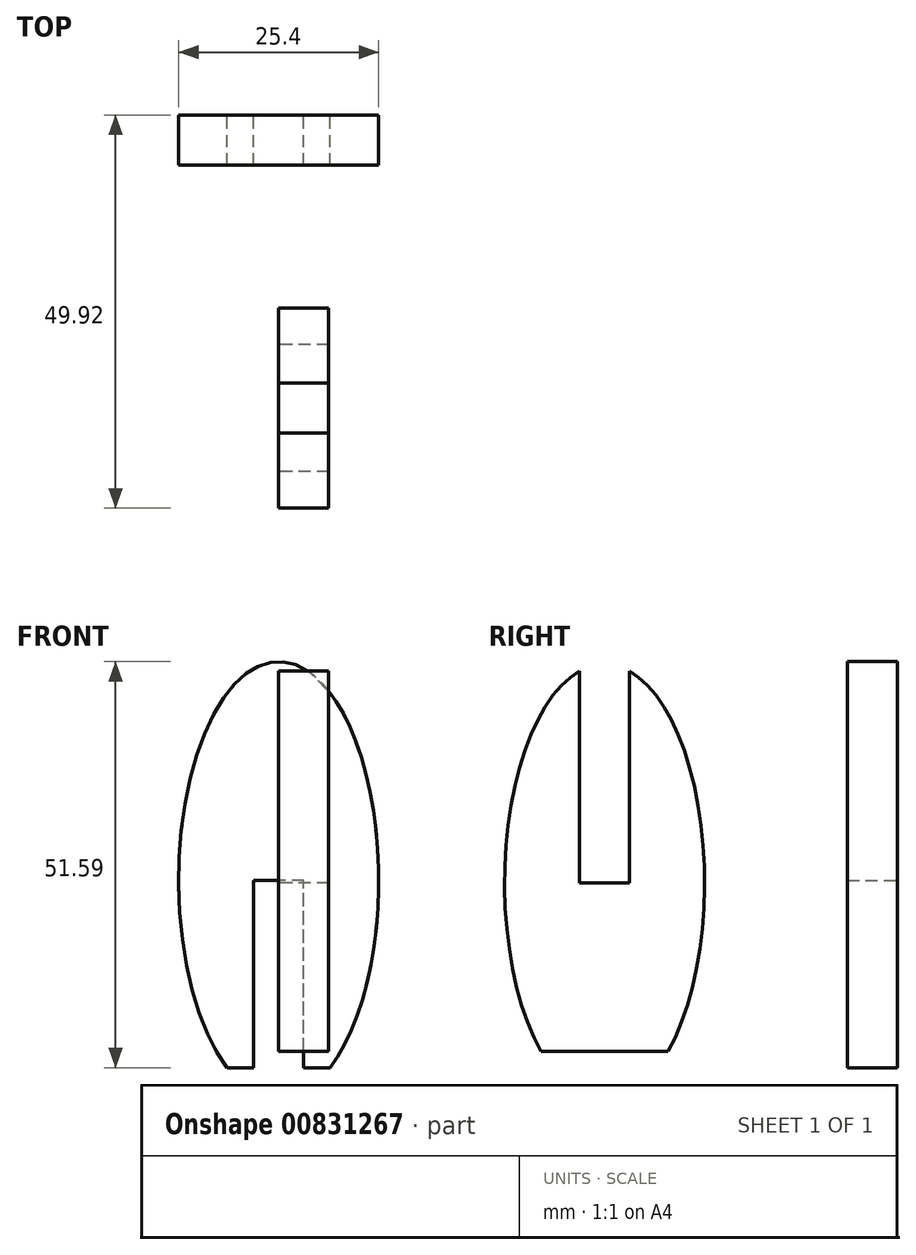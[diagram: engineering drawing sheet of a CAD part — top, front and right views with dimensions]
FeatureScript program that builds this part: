
annotation { "Feature Type Name" : "Feature", "Feature Type Description" : "" }
export const myFeature = defineFeature(function(context is Context, id is Id, definition is map)
    precondition{}
    {
        {
            var Q0;
            Q0=qCreatedBy(makeId("Front.planeOp"),FACE);
            var sketch = newSketch(context, id + "F0", { "sketchPlane" : qUnion([Q0])});
            skEllipse(sketch, "E0", {"center": v(0, 45.44) * mm, "majorRadius": 27.78 * mm, "minorRadius": 12.7 * mm, "majorAxis": v(0, -1)});
            skLineSegment(sketch, "E1.bottom", {"start": v(3.81, 17.66) * mm, "end": v(-2.54, 17.66) * mm});
            skLineSegment(sketch, "E1.top", {"start": v(3.18, 45.44) * mm, "end": v(-3.17, 45.44) * mm});
            skLineSegment(sketch, "E1.left", {"start": v(3.18, 17.66) * mm, "end": v(3.18, 45.44) * mm});
            skLineSegment(sketch, "E1.right", {"start": v(-3.17, 17.66) * mm, "end": v(-3.17, 45.44) * mm});
            skLineSegment(sketch, "E2.bottom", {"start": v(12.7, 17.66) * mm, "end": v(-12.7, 17.66) * mm});
            skLineSegment(sketch, "E2.top", {"start": v(12.7, 21.63) * mm, "end": v(-12.7, 21.63) * mm});
            skLineSegment(sketch, "E2.left", {"start": v(12.7, 17.66) * mm, "end": v(12.7, 21.63) * mm});
            skLineSegment(sketch, "E2.right", {"start": v(-12.7, 17.66) * mm, "end": v(-12.7, 21.63) * mm});
            skSolve(sketch);
        }
        {
            var Q0;
            {var subQ5=sQuery(id+"F0.wireOp",EDGE,"E1.top");Q0=makeQuery(id+"F0.imprint","IMPRINT",FACE,{"disambiguationData":[TD([[makeQuery(id+"F0.imprint","IMPRINT",EDGE,{"derivedFrom":subQ5}),-1.0]])]});}
            extrude(context, id + "F1", {"entities" : qUnion([Q0]), "depth" : 6.35 * mm, "offsetDistance" : 25.4 * mm});
        }
        {
            var Q0;
            Q0=qCreatedBy(makeId("Right.planeOp"),FACE);
            var sketch = newSketch(context, id + "F2", { "sketchPlane" : qUnion([Q0])});
            skEllipse(sketch, "E3", {"center": v(-37.22, 45.12) * mm, "majorRadius": 27.78 * mm, "minorRadius": 12.7 * mm, "majorAxis": v(0, 1)});
            skLineSegment(sketch, "E4.top", {"start": v(-40.4, 45.1) * mm, "end": v(-34.05, 45.1) * mm});
            skLineSegment(sketch, "E4.left", {"start": v(-40.4, 72.9) * mm, "end": v(-40.4, 45.1) * mm});
            skLineSegment(sketch, "E4.right", {"start": v(-34.05, 72.9) * mm, "end": v(-34.05, 45.1) * mm});
            skLineSegment(sketch, "E5", {"start": v(-34.05, 72.9) * mm, "end": v(-40.4, 72.9) * mm});
            skLineSegment(sketch, "E6.bottom", {"start": v(-49.91, 17.33) * mm, "end": v(-24.51, 17.33) * mm});
            skLineSegment(sketch, "E6.top", {"start": v(-49.91, 23.68) * mm, "end": v(-24.51, 23.68) * mm});
            skLineSegment(sketch, "E6.left", {"start": v(-49.91, 17.33) * mm, "end": v(-49.91, 23.68) * mm});
            skLineSegment(sketch, "E6.right", {"start": v(-24.51, 17.33) * mm, "end": v(-24.51, 23.68) * mm});
            skSolve(sketch);
        }
        {
            var Q0;
            {var subQ1=sQuery(id+"F2.wireOp",EDGE,"E4.top");Q0=makeQuery(id+"F2.imprint","IMPRINT",FACE,{"disambiguationData":[TD([[makeQuery(id+"F2.imprint","IMPRINT",EDGE,{"derivedFrom":subQ1}),-1.0]])]});}
            extrude(context, id + "F3", {"entities" : qUnion([Q0]), "depth" : 6.35 * mm, "offsetDistance" : 25.4 * mm});
        }
    });
